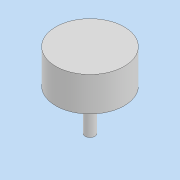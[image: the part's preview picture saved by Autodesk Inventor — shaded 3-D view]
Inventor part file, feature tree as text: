
AUTODESK INVENTOR PART (.ipt)
format: ipt  version: 2022 (Build 260153070, 153G)  size: 101,376 bytes
history: native  units: mm
features: revolve x1, sketch x1
ambient origin geometry x8: Origin, YZ Plane, XZ Plane, XY Plane, X Axis, Y Axis, Z Axis, Center Point
bodies: Solid1 (feature_tree)
feature tree (2):
  revolve  "Revolution1"  [1 undecoded]
  sketch  "Sketch1"  dims[d0=1.45mm d1=8.0mm d2=11.34464mm d4=10.0mm d5=90.0deg d6=10.0mm]
note: 1 required parameter value undecoded (feature->parameter linkage not recoverable at this tier; creation-order binding heuristic only, values carry confidence <= 0.55)
